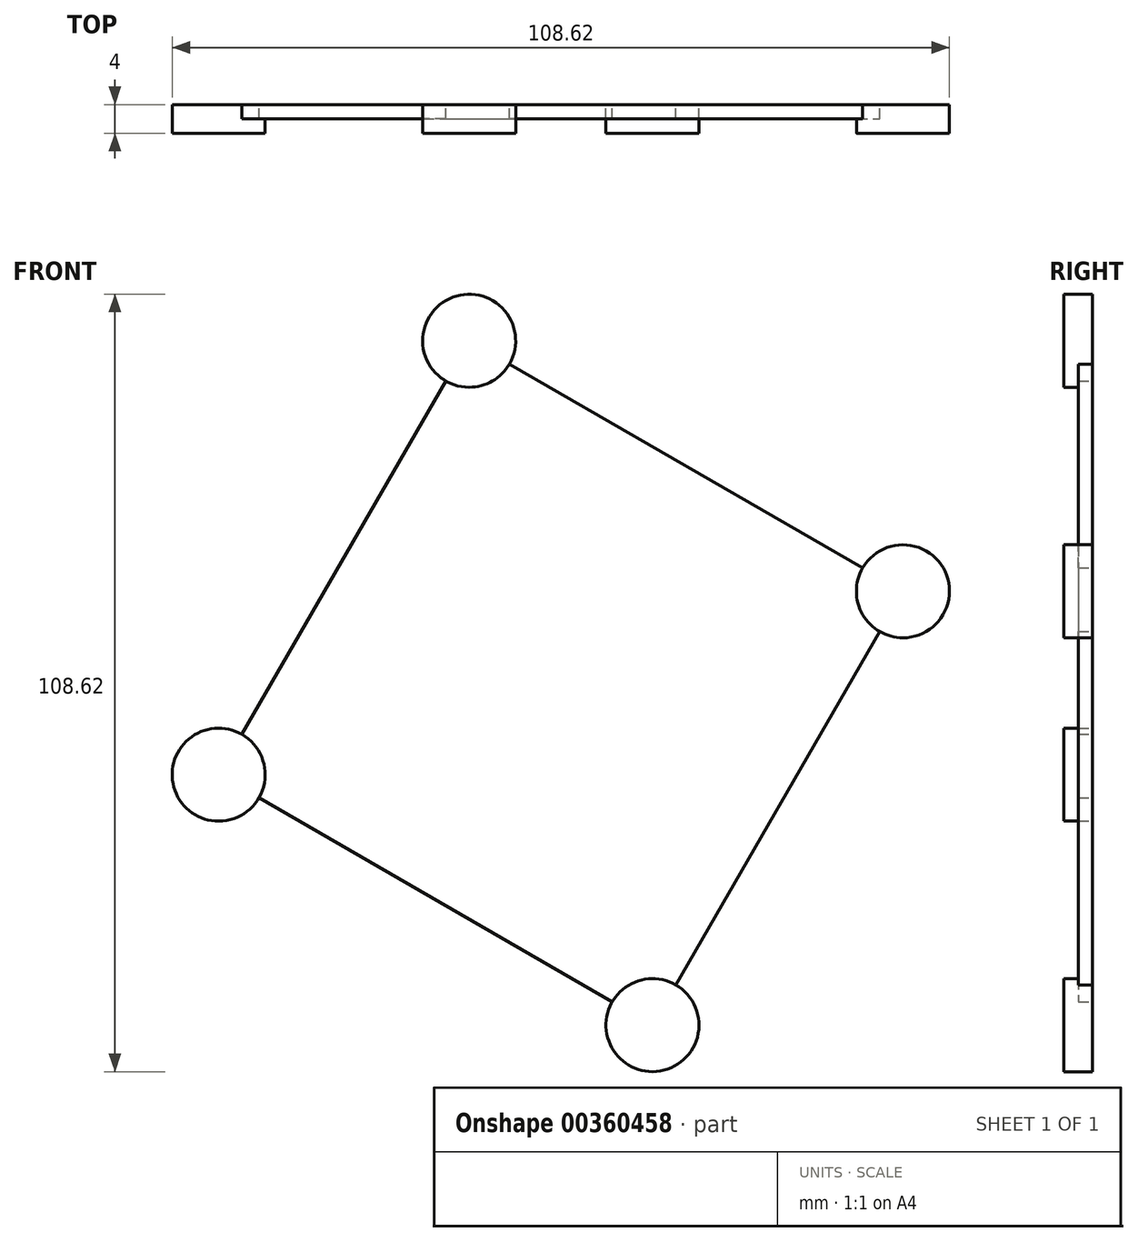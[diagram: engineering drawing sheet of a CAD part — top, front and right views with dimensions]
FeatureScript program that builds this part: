
annotation { "Feature Type Name" : "Feature", "Feature Type Description" : "" }
export const myFeature = defineFeature(function(context is Context, id is Id, definition is map)
    precondition{}
    {
        {
            var Q0;
            Q0=qCreatedBy(makeId("Front.planeOp"),FACE);
            var sketch = newSketch(context, id + "F0", { "sketchPlane" : qUnion([Q0])});
            skLineSegment(sketch, "E0", {"start": v(12.81, -47.81) * mm, "end": v(47.81, 12.81) * mm});
            skLineSegment(sketch, "E1", {"start": v(47.81, 12.81) * mm, "end": v(-12.81, 47.81) * mm});
            skLineSegment(sketch, "E2", {"start": v(-12.81, 47.81) * mm, "end": v(-47.81, -12.81) * mm});
            skLineSegment(sketch, "E3", {"start": v(-47.81, -12.81) * mm, "end": v(12.81, -47.81) * mm});
            skLineSegment(sketch, "E4", {"start": v(-47.81, -12.81) * mm, "end": v(47.81, 12.81) * mm, "construction": true});
            skCircle(sketch, "E5", {"center": v(-47.81, -12.81) * mm, "radius": 6.5 * mm});
            skCircle(sketch, "E6", {"center": v(-12.81, 47.81) * mm, "radius": 6.5 * mm});
            skCircle(sketch, "E7", {"center": v(47.81, 12.81) * mm, "radius": 6.5 * mm});
            skCircle(sketch, "E8", {"center": v(12.81, -47.81) * mm, "radius": 6.5 * mm});
            skSolve(sketch);
        }
        {
            var Q0;
            {var subQ3=sQuery(id+"F0.wireOp",EDGE,"E8");var subQ9=sQuery(id+"F0.wireOp",EDGE,"E0");var subQ10=makeQuery(id+"F0.imprint","INTERSECT",VERTEX,{"derivedFrom":[subQ9,subQ3]});Q0=makeQuery(id+"F0.imprint","IMPRINT",FACE,{"disambiguationData":[TD([[makeQuery(id+"F0.imprint","IMPRINT",EDGE,{"disambiguationData":[TD([[subQ10,-1.0]])],"derivedFrom":subQ9}),1.0]])]});}
            extrude(context, id + "F1", {"entities" : qUnion([Q0]), "depth" : 2 * mm});
        }
        {
            var Q0;
            {var subQ0=sQuery(id+"F0.wireOp",EDGE,"E3");var subQ1=sQuery(id+"F0.wireOp",EDGE,"E2");var subQ2=makeQuery(id+"F0.imprint","INTERSECT",VERTEX,{"derivedFrom":[subQ1,subQ0]});Q0=makeQuery(id+"F0.imprint","IMPRINT",FACE,{"disambiguationData":[TD([[makeQuery(id+"F0.imprint","IMPRINT",EDGE,{"disambiguationData":[TD([[subQ2,1.0]])],"derivedFrom":subQ1}),1.0]])]});}
            var Q1;
            {var subQ0=sQuery(id+"F0.wireOp",EDGE,"E3");var subQ1=sQuery(id+"F0.wireOp",EDGE,"E2");var subQ2=makeQuery(id+"F0.imprint","INTERSECT",VERTEX,{"derivedFrom":[subQ1,subQ0]});Q1=makeQuery(id+"F0.imprint","IMPRINT",FACE,{"disambiguationData":[TD([[makeQuery(id+"F0.imprint","IMPRINT",EDGE,{"disambiguationData":[TD([[subQ2,1.0]])],"derivedFrom":subQ1}),-1.0]])]});}
            var Q2;
            {var subQ0=sQuery(id+"F0.wireOp",EDGE,"E3");var subQ1=sQuery(id+"F0.wireOp",EDGE,"E0");var subQ2=makeQuery(id+"F0.imprint","INTERSECT",VERTEX,{"derivedFrom":[subQ1,subQ0]});Q2=makeQuery(id+"F0.imprint","IMPRINT",FACE,{"disambiguationData":[TD([[makeQuery(id+"F0.imprint","IMPRINT",EDGE,{"disambiguationData":[TD([[subQ2,-1.0]])],"derivedFrom":subQ1}),-1.0]])]});}
            var Q3;
            {var subQ0=sQuery(id+"F0.wireOp",EDGE,"E3");var subQ1=sQuery(id+"F0.wireOp",EDGE,"E0");var subQ2=makeQuery(id+"F0.imprint","INTERSECT",VERTEX,{"derivedFrom":[subQ1,subQ0]});Q3=makeQuery(id+"F0.imprint","IMPRINT",FACE,{"disambiguationData":[TD([[makeQuery(id+"F0.imprint","IMPRINT",EDGE,{"disambiguationData":[TD([[subQ2,-1.0]])],"derivedFrom":subQ1}),1.0]])]});}
            var Q4;
            {var subQ0=sQuery(id+"F0.wireOp",EDGE,"E1");var subQ1=sQuery(id+"F0.wireOp",EDGE,"E0");var subQ2=makeQuery(id+"F0.imprint","INTERSECT",VERTEX,{"derivedFrom":[subQ1,subQ0]});Q4=makeQuery(id+"F0.imprint","IMPRINT",FACE,{"disambiguationData":[TD([[makeQuery(id+"F0.imprint","IMPRINT",EDGE,{"disambiguationData":[TD([[subQ2,1.0]])],"derivedFrom":subQ1}),1.0]])]});}
            var Q5;
            {var subQ0=sQuery(id+"F0.wireOp",EDGE,"E1");var subQ1=sQuery(id+"F0.wireOp",EDGE,"E0");var subQ2=makeQuery(id+"F0.imprint","INTERSECT",VERTEX,{"derivedFrom":[subQ1,subQ0]});Q5=makeQuery(id+"F0.imprint","IMPRINT",FACE,{"disambiguationData":[TD([[makeQuery(id+"F0.imprint","IMPRINT",EDGE,{"disambiguationData":[TD([[subQ2,1.0]])],"derivedFrom":subQ1}),-1.0]])]});}
            var Q6;
            {var subQ0=sQuery(id+"F0.wireOp",EDGE,"E2");var subQ1=sQuery(id+"F0.wireOp",EDGE,"E1");var subQ2=makeQuery(id+"F0.imprint","INTERSECT",VERTEX,{"derivedFrom":[subQ1,subQ0]});Q6=makeQuery(id+"F0.imprint","IMPRINT",FACE,{"disambiguationData":[TD([[makeQuery(id+"F0.imprint","IMPRINT",EDGE,{"disambiguationData":[TD([[subQ2,1.0]])],"derivedFrom":subQ1}),1.0]])]});}
            var Q7;
            {var subQ0=sQuery(id+"F0.wireOp",EDGE,"E2");var subQ1=sQuery(id+"F0.wireOp",EDGE,"E1");var subQ2=makeQuery(id+"F0.imprint","INTERSECT",VERTEX,{"derivedFrom":[subQ1,subQ0]});Q7=makeQuery(id+"F0.imprint","IMPRINT",FACE,{"disambiguationData":[TD([[makeQuery(id+"F0.imprint","IMPRINT",EDGE,{"disambiguationData":[TD([[subQ2,1.0]])],"derivedFrom":subQ1}),-1.0]])]});}
            extrude(context, id + "F2", {"entities" : qUnion([Q0, Q1, Q2, Q3, Q4, Q5, Q6, Q7]), "operationType" : NewBodyOperationType.ADD, "depth" : 4 * mm});
        }
    });
